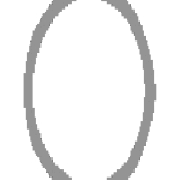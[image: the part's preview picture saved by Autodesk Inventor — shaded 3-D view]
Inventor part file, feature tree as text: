
AUTODESK INVENTOR PART (.ipt)
format: ipt  version: 2021 (Build 250183000, 183)  size: 113,152 bytes
history: native  units: in
note: dims shown in document units (in); Inventor stores cm internally (conversion verified against a paired STEP export)
features: other x4, sketch x3, plane x1
ambient origin geometry x8: Origin, YZ Plane, XZ Plane, XY Plane, X Axis, Y Axis, Z Axis, Center Point
bodies: Solid1 (feature_tree), Body (feature_tree)
feature tree (8):
  other  "Driven Length"
  other  "Frame Generator"
  other  "Start Plane"
  other  "End Plane"
  sketch  "Sketch"  dims[d2=12.0in d4=-0.0in d5=12.0in d6=0.12in d7=0.0in d8=90.0deg d9=12.0in]
  sketch  "Sketch2"  dims[d0=1.0in]
  plane  "Work Plane3"
  sketch  "Sketch3"  dims[d1=0.065in]
